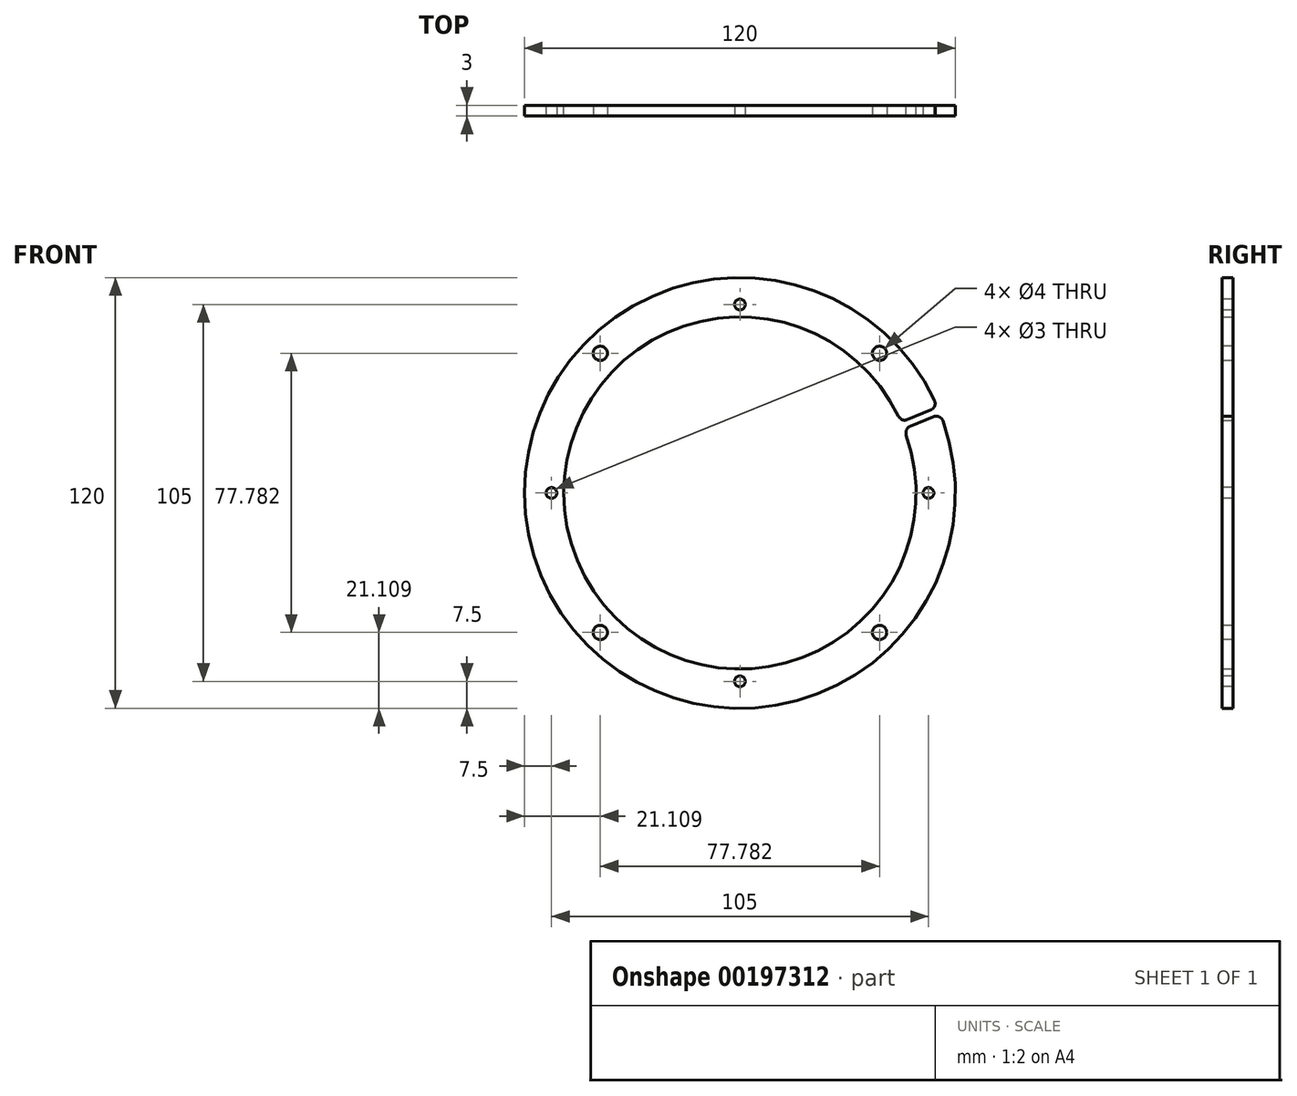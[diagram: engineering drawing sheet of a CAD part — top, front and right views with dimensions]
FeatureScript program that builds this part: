
annotation { "Feature Type Name" : "Feature", "Feature Type Description" : "" }
export const myFeature = defineFeature(function(context is Context, id is Id, definition is map)
    precondition{}
    {
        {
            var Q0;
            Q0=qCreatedBy(makeId("Front.planeOp"),FACE);
            var sketch = newSketch(context, id + "F0", { "sketchPlane" : qUnion([Q0])});
            skCircle(sketch, "E0", {"center": v(0, 0) * mm, "radius": 49.05 * mm});
            skCircle(sketch, "E1", {"center": v(0, 0) * mm, "radius": 60 * mm});
            skSolve(sketch);
        }
        {
            var Q0;
            Q0 = qSketchRegion(id + "F0", true);
            extrude(context, id + "F1", {"entities" : qUnion([Q0]), "depth" : 3 * mm});
        }
        {
            var Q0;
            Q0=makeQuery(id+"F1.opExtrude","CAP_FACE",FACE,{"disambiguationData":[OSD([sQuery(id+"F0.wireOp",EDGE,"E0"),sQuery(id+"F0.wireOp",EDGE,"E1")])],"isStart":false});
            var sketch = newSketch(context, id + "F2", { "sketchPlane" : qUnion([Q0])});
            skLineSegment(sketch, "E2", {"start": v(0, 0) * mm, "end": v(0, 60) * mm, "construction": true});
            skLineSegment(sketch, "E3", {"start": v(0, 0) * mm, "end": v(-60, 0) * mm, "construction": true});
            skCircle(sketch, "E4", {"center": v(-52.5, 0) * mm, "radius": 1.5 * mm});
            skCircle(sketch, "E5", {"center": v(0, 52.5) * mm, "radius": 1.5 * mm});
            skCircle(sketch, "E6.MirrorC", {"center": v(52.5, 0) * mm, "radius": 1.5 * mm});
            skCircle(sketch, "E7.MirrorC", {"center": v(0, -52.5) * mm, "radius": 1.5 * mm});
            skLineSegment(sketch, "E8", {"start": v(0, 0) * mm, "end": v(55.43, 22.96) * mm, "construction": true});
            skLineSegment(sketch, "E9", {"start": v(40.31, 17.78) * mm, "end": v(59.67, 25.8) * mm});
            skLineSegment(sketch, "E10", {"start": v(59.67, 25.8) * mm, "end": v(60.05, 24.87) * mm});
            skLineSegment(sketch, "E11", {"start": v(40.31, 17.78) * mm, "end": v(40.7, 16.86) * mm});
            skLineSegment(sketch, "E12.MirrorCS", {"start": v(41.08, 15.93) * mm, "end": v(40.7, 16.86) * mm});
            skLineSegment(sketch, "E13.MirrorCS", {"start": v(41.08, 15.93) * mm, "end": v(60.43, 23.95) * mm});
            skLineSegment(sketch, "E14.MirrorCS", {"start": v(60.43, 23.95) * mm, "end": v(60.05, 24.87) * mm});
            skCircle(sketch, "E15", {"center": v(0, 0) * mm, "radius": 52.5 * mm, "construction": true});
            skCircle(sketch, "E16", {"center": v(-38.9, 38.9) * mm, "radius": 2 * mm});
            skLineSegment(sketch, "E17", {"start": v(0, 0) * mm, "end": v(-42.43, 42.43) * mm, "construction": true});
            skCircle(sketch, "E18.1.0", {"center": v(-38.9, -38.9) * mm, "radius": 2 * mm});
            skCircle(sketch, "E18.2.0", {"center": v(38.9, -38.9) * mm, "radius": 2 * mm});
            skCircle(sketch, "E18.3.0", {"center": v(38.9, 38.9) * mm, "radius": 2 * mm});
            skCircle(sketch, "E19", {"center": v(0, 0) * mm, "radius": 55 * mm, "construction": true});
            skSolve(sketch);
        }
        {
            var Q0;
            Q0 = qSketchRegion(id + "F2", true);
            extrude(context, id + "F3", {"entities" : qUnion([Q0]), "operationType" : NewBodyOperationType.REMOVE, "endBound" : BoundingType.THROUGH_ALL, "oppositeDirection" : true, "depth" : 25 * mm});
        }
        {
            var Q0;
            Q0=makeQuery(id+"F3.boolean.opBoolean","INTERSECT",EDGE,{"derivedFrom":[makeQuery(id+"F1.opExtrude","SWEPT_FACE",FACE,{"disambiguationData":[OSD([sQuery(id+"F0.wireOp",EDGE,"E1")])]}),makeQuery(id+"F3.opExtrude","SWEPT_FACE",FACE,{"disambiguationData":[OSD([sQuery(id+"F2.wireOp",EDGE,"E9")])]})]});
            var Q1;
            Q1=makeQuery(id+"F3.boolean.opBoolean","INTERSECT",EDGE,{"derivedFrom":[makeQuery(id+"F1.opExtrude","SWEPT_FACE",FACE,{"disambiguationData":[OSD([sQuery(id+"F0.wireOp",EDGE,"E1")])]}),makeQuery(id+"F3.opExtrude","SWEPT_FACE",FACE,{"disambiguationData":[OSD([sQuery(id+"F2.wireOp",EDGE,"E13.MirrorCS")])]})]});
            var Q2;
            Q2=makeQuery(id+"F3.boolean.opBoolean","INTERSECT",EDGE,{"derivedFrom":[makeQuery(id+"F1.opExtrude","SWEPT_FACE",FACE,{"disambiguationData":[OSD([sQuery(id+"F0.wireOp",EDGE,"E0")])]}),makeQuery(id+"F3.opExtrude","SWEPT_FACE",FACE,{"disambiguationData":[OSD([sQuery(id+"F2.wireOp",EDGE,"E9")])]})]});
            var Q3;
            Q3=makeQuery(id+"F3.boolean.opBoolean","INTERSECT",EDGE,{"derivedFrom":[makeQuery(id+"F1.opExtrude","SWEPT_FACE",FACE,{"disambiguationData":[OSD([sQuery(id+"F0.wireOp",EDGE,"E0")])]}),makeQuery(id+"F3.opExtrude","SWEPT_FACE",FACE,{"disambiguationData":[OSD([sQuery(id+"F2.wireOp",EDGE,"E13.MirrorCS")])]})]});
            fillet(context, id + "F4", {"entities" : qUnion([Q0, Q1, Q2, Q3]), "radius" : 2 * mm, "tangentPropagation" : true, "allowEdgeOverflow" : false});
        }
    });
